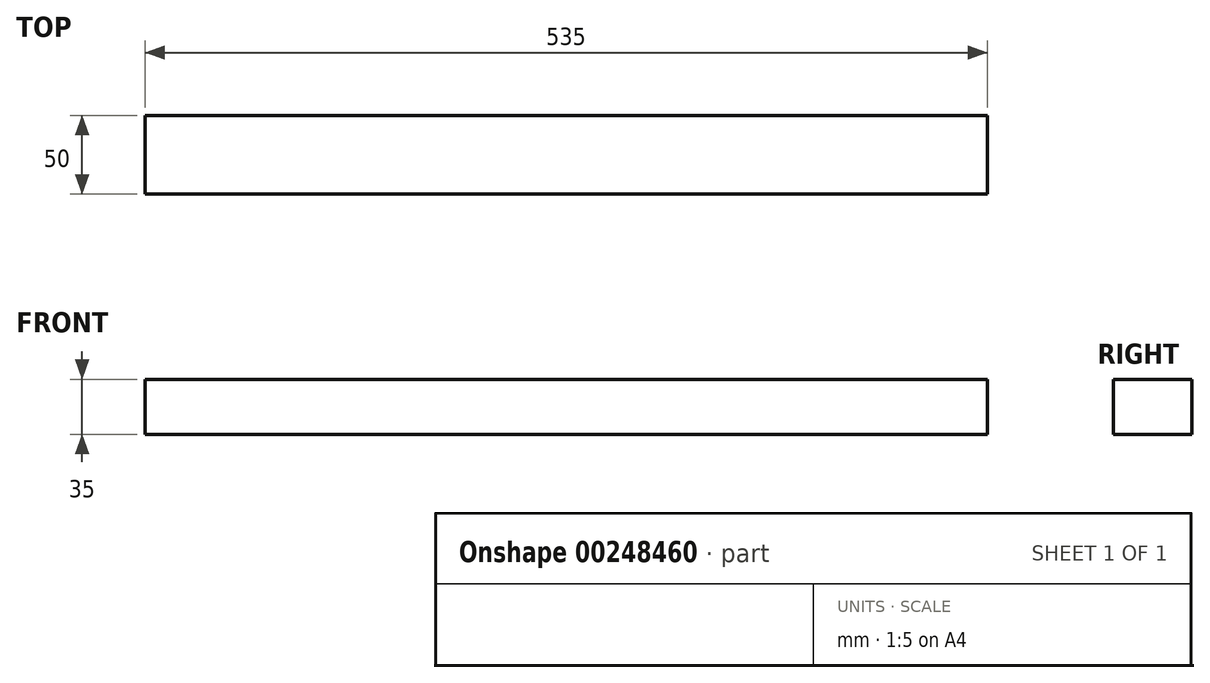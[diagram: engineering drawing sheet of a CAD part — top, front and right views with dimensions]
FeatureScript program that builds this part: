
annotation { "Feature Type Name" : "Feature", "Feature Type Description" : "" }
export const myFeature = defineFeature(function(context is Context, id is Id, definition is map)
    precondition{}
    {
        {
            var Q0;
            Q0=qCreatedBy(makeId("Right.planeOp"),FACE);
            var sketch = newSketch(context, id + "F0", { "sketchPlane" : qUnion([Q0])});
            skLineSegment(sketch, "E0.bottom", {"start": v(25, 17.5) * mm, "end": v(-25, 17.5) * mm});
            skLineSegment(sketch, "E0.top", {"start": v(25, -17.5) * mm, "end": v(-25, -17.5) * mm});
            skLineSegment(sketch, "E0.left", {"start": v(25, 17.5) * mm, "end": v(25, -17.5) * mm});
            skLineSegment(sketch, "E0.right", {"start": v(-25, 17.5) * mm, "end": v(-25, -17.5) * mm});
            skPoint(sketch, "E0.middle", {"position": v(0, 0) * mm});
            skSolve(sketch);
        }
        {
            var Q0;
            Q0 = qSketchRegion(id + "F0", true);
            extrude(context, id + "F1", {"entities" : qUnion([Q0]), "endBound" : BoundingType.SYMMETRIC, "depth" : 535 * mm});
        }
    });
